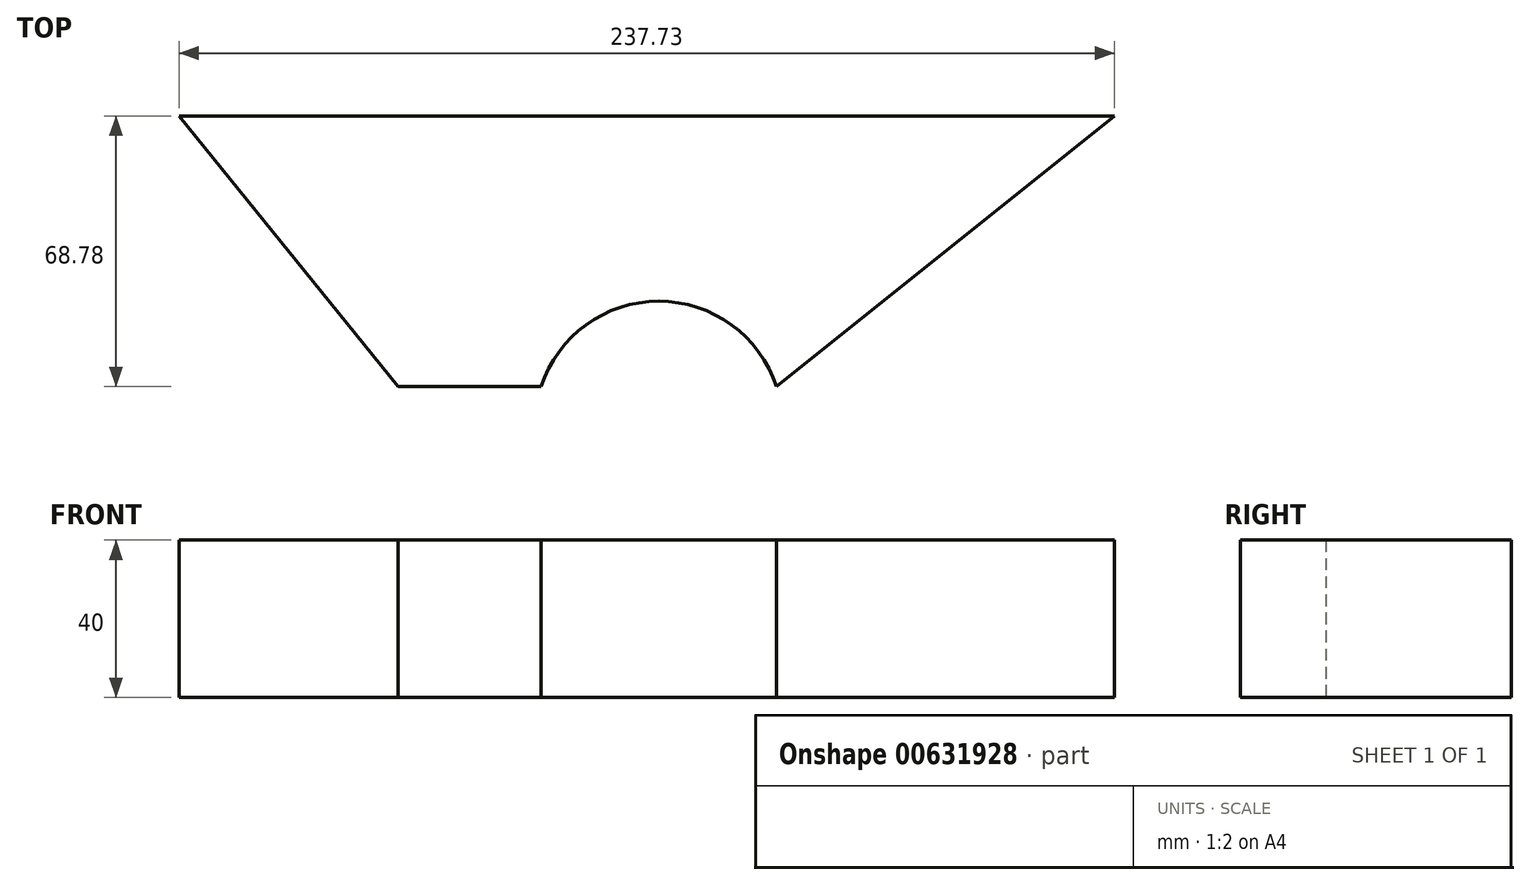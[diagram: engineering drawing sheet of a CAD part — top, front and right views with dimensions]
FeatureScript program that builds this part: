
annotation { "Feature Type Name" : "Feature", "Feature Type Description" : "" }
export const myFeature = defineFeature(function(context is Context, id is Id, definition is map)
    precondition{}
    {
        {
            var Q0;
            Q0=qCreatedBy(makeId("Front.planeOp"),FACE);
            var sketch = newSketch(context, id + "F0", { "sketchPlane" : qUnion([Q0])});
            skLineSegment(sketch, "E0.bottom", {"start": v(5, 30) * mm, "end": v(-5, 30) * mm});
            skLineSegment(sketch, "E0.top", {"start": v(5, 45) * mm, "end": v(-5, 45) * mm});
            skLineSegment(sketch, "E0.left", {"start": v(5, 30) * mm, "end": v(5, 45) * mm});
            skLineSegment(sketch, "E0.right", {"start": v(-5, 30) * mm, "end": v(-5, 45) * mm});
            skPoint(sketch, "E0.middle", {"position": v(0, 37.5) * mm});
            skSolve(sketch);
        }
        {
            var Q0;
            Q0=qCreatedBy(makeId("Top.planeOp"),FACE);
            var sketch = newSketch(context, id + "F1", { "sketchPlane" : qUnion([Q0])});
            skArc(sketch, "E1", {"start": v(29.94, 0) * mm, "mid": v(0, 21.7) * mm, "end": v(-29.94, 0) * mm});
            skLineSegment(sketch, "E2", {"start": v(-29.94, 0) * mm, "end": v(-66.2, 0) * mm});
            skLineSegment(sketch, "E3", {"start": v(-66.2, 0) * mm, "end": v(-121.92, 68.78) * mm});
            skLineSegment(sketch, "E4", {"start": v(-121.92, 68.78) * mm, "end": v(115.81, 68.78) * mm});
            skLineSegment(sketch, "E5", {"start": v(115.81, 68.78) * mm, "end": v(29.94, 0) * mm});
            skSolve(sketch);
        }
        {
            var Q0;
            Q0 = qSketchRegion(id + "F1", true);
            extrude(context, id + "F2", {"entities" : qUnion([Q0]), "depth" : 40 * mm, "offsetDistance" : 25 * mm});
        }
    });
